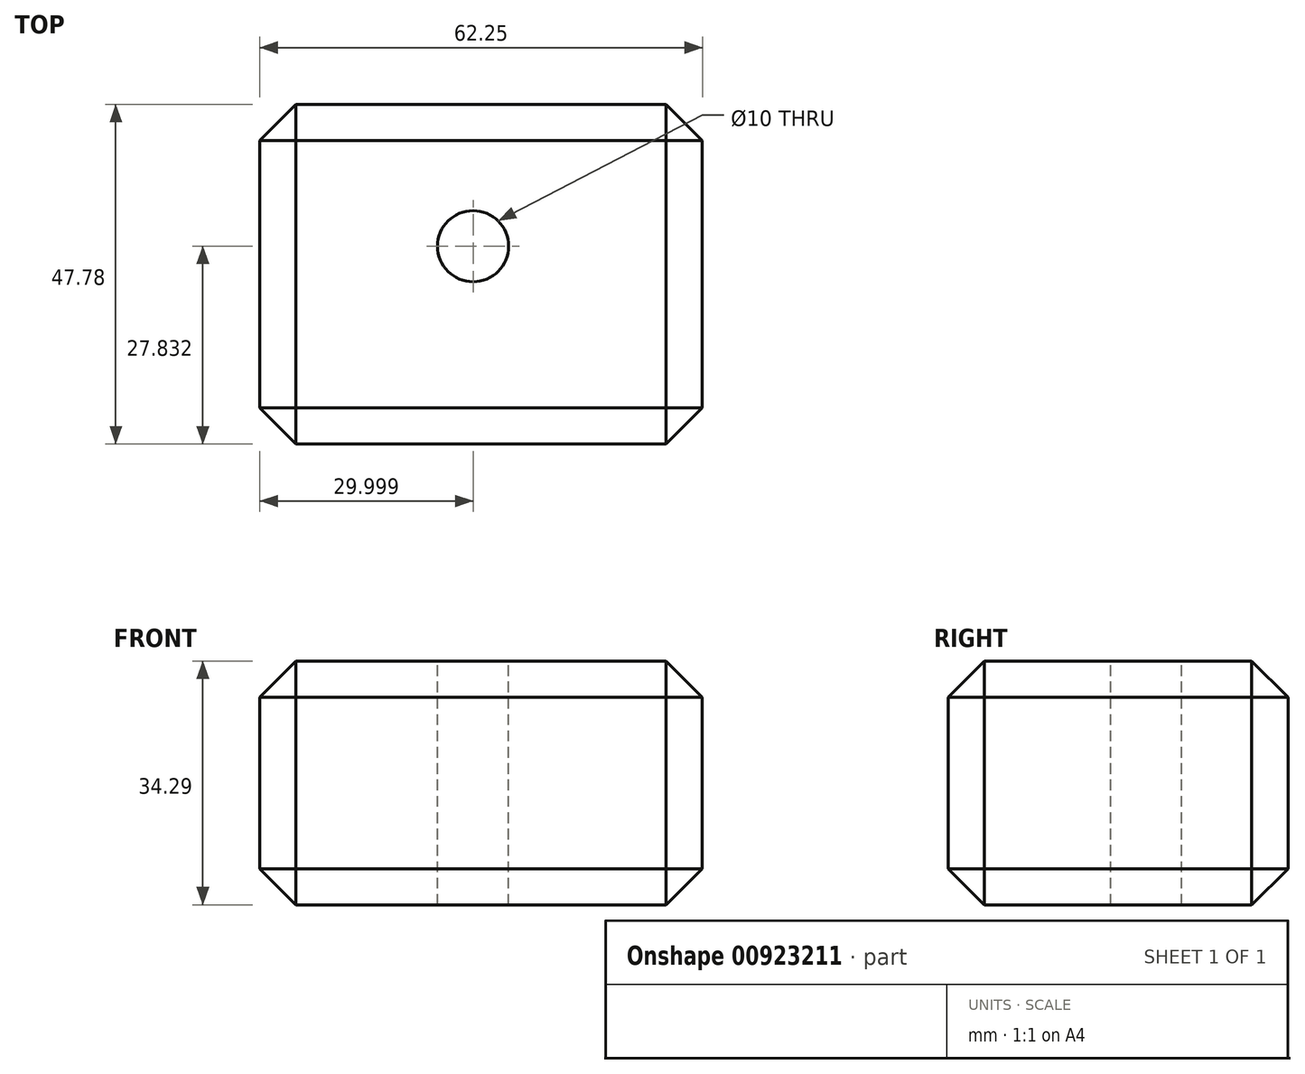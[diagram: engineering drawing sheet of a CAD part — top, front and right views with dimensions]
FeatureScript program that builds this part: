
annotation { "Feature Type Name" : "Feature", "Feature Type Description" : "" }
export const myFeature = defineFeature(function(context is Context, id is Id, definition is map)
    precondition{}
    {
        {
            var Q0;
            Q0=qCreatedBy(makeId("Top.planeOp"),FACE);
            var sketch = newSketch(context, id + "F0", { "sketchPlane" : qUnion([Q0])});
            skLineSegment(sketch, "E0.bottom", {"start": v(-116.22, 0) * mm, "end": v(-53.97, 0) * mm});
            skLineSegment(sketch, "E0.top", {"start": v(-116.22, -47.78) * mm, "end": v(-53.97, -47.78) * mm});
            skLineSegment(sketch, "E0.left", {"start": v(-116.22, 0) * mm, "end": v(-116.22, -47.78) * mm});
            skLineSegment(sketch, "E0.right", {"start": v(-53.97, 0) * mm, "end": v(-53.97, -47.78) * mm});
            skSolve(sketch);
        }
        {
            var Q0;
            Q0=makeQuery(id+"F0.imprint","IMPRINT",FACE,{"disambiguationData":[TD([[makeQuery(id+"F0.imprint","IMPRINT",EDGE,{"derivedFrom":sQuery(id+"F0.wireOp",EDGE,"E0.bottom")}),-1.0]])]});
            extrude(context, id + "F1", {"entities" : qUnion([Q0]), "depth" : 34.3 * mm, "offsetDistance" : 25.4 * mm});
        }
        {
            var Q0;
            Q0=makeQuery(id+"F1.opExtrude","SWEPT_FACE",FACE,{"disambiguationData":[OSD([sQuery(id+"F0.wireOp",EDGE,"E0.top")])]});
            var Q1;
            Q1=makeQuery(id+"F1.opExtrude","CAP_FACE",FACE,{"disambiguationData":[OSD([sQuery(id+"F0.wireOp",EDGE,"E0.bottom"),sQuery(id+"F0.wireOp",EDGE,"E0.top"),sQuery(id+"F0.wireOp",EDGE,"E0.left"),sQuery(id+"F0.wireOp",EDGE,"E0.right")])],"isStart":false});
            var Q2;
            Q2=makeQuery(id+"F1.opExtrude","SWEPT_FACE",FACE,{"disambiguationData":[OSD([sQuery(id+"F0.wireOp",EDGE,"E0.right")])]});
            var Q3;
            Q3=makeQuery(id+"F1.opExtrude","SWEPT_FACE",FACE,{"disambiguationData":[OSD([sQuery(id+"F0.wireOp",EDGE,"E0.left")])]});
            var Q4;
            Q4=makeQuery(id+"F1.opExtrude","CAP_FACE",FACE,{"disambiguationData":[OSD([sQuery(id+"F0.wireOp",EDGE,"E0.bottom"),sQuery(id+"F0.wireOp",EDGE,"E0.top"),sQuery(id+"F0.wireOp",EDGE,"E0.left"),sQuery(id+"F0.wireOp",EDGE,"E0.right")])],"isStart":true});
            var Q5;
            Q5=makeQuery(id+"F1.opExtrude","SWEPT_FACE",FACE,{"disambiguationData":[OSD([sQuery(id+"F0.wireOp",EDGE,"E0.bottom")])]});
            chamfer(context, id + "F2", {"entities" : qUnion([Q0, Q1, Q2, Q3, Q4, Q5]), "width" : 5.08 * mm, "tangentPropagation" : true});
        }
        {
            var Q0;
            Q0=makeQuery(id+"F1.opExtrude","CAP_FACE",FACE,{"disambiguationData":[OSD([sQuery(id+"F0.wireOp",EDGE,"E0.bottom"),sQuery(id+"F0.wireOp",EDGE,"E0.top"),sQuery(id+"F0.wireOp",EDGE,"E0.left"),sQuery(id+"F0.wireOp",EDGE,"E0.right")])],"isStart":false});
            var sketch = newSketch(context, id + "F3", { "sketchPlane" : qUnion([Q0])});
            skPoint(sketch, "E1", {"position": v(-86.22, -19.95) * mm});
            skSolve(sketch);
        }
        {
            var Q0;
            Q0=sQuery(id+"F3.wireOp",VERTEX,"E1");
            var Q1;
            Q1=makeQuery(id+"F1.opExtrude","SWEPT_BODY",BODY,{"disambiguationData":[OSD([sQuery(id+"F0.wireOp",EDGE,"E0.bottom"),sQuery(id+"F0.wireOp",EDGE,"E0.top"),sQuery(id+"F0.wireOp",EDGE,"E0.left"),sQuery(id+"F0.wireOp",EDGE,"E0.right")])]});
            hole(context, id + "F4", {"style" : HoleStyle.SIMPLE, "endStyle" : HoleEndStyle.THROUGH, "standardTappedOrClearance" : lookupTablePath({ "standard" : "ISO", "size" : "10", "type" : "Drilled" }), "standardBlindInLast" : lookupTablePath({ "standard" : "ISO", "size" : "10", "type" : "Drilled" }), "holeDiameter" : 10 * mm, "majorDiameter" : 6.35 * mm, "isTappedThrough" : true, "tappedDepth" : 12.7 * mm, "tapClearance" : 3, "locations" : qUnion([Q0]), "scope" : qUnion([Q1])});
        }
    });
